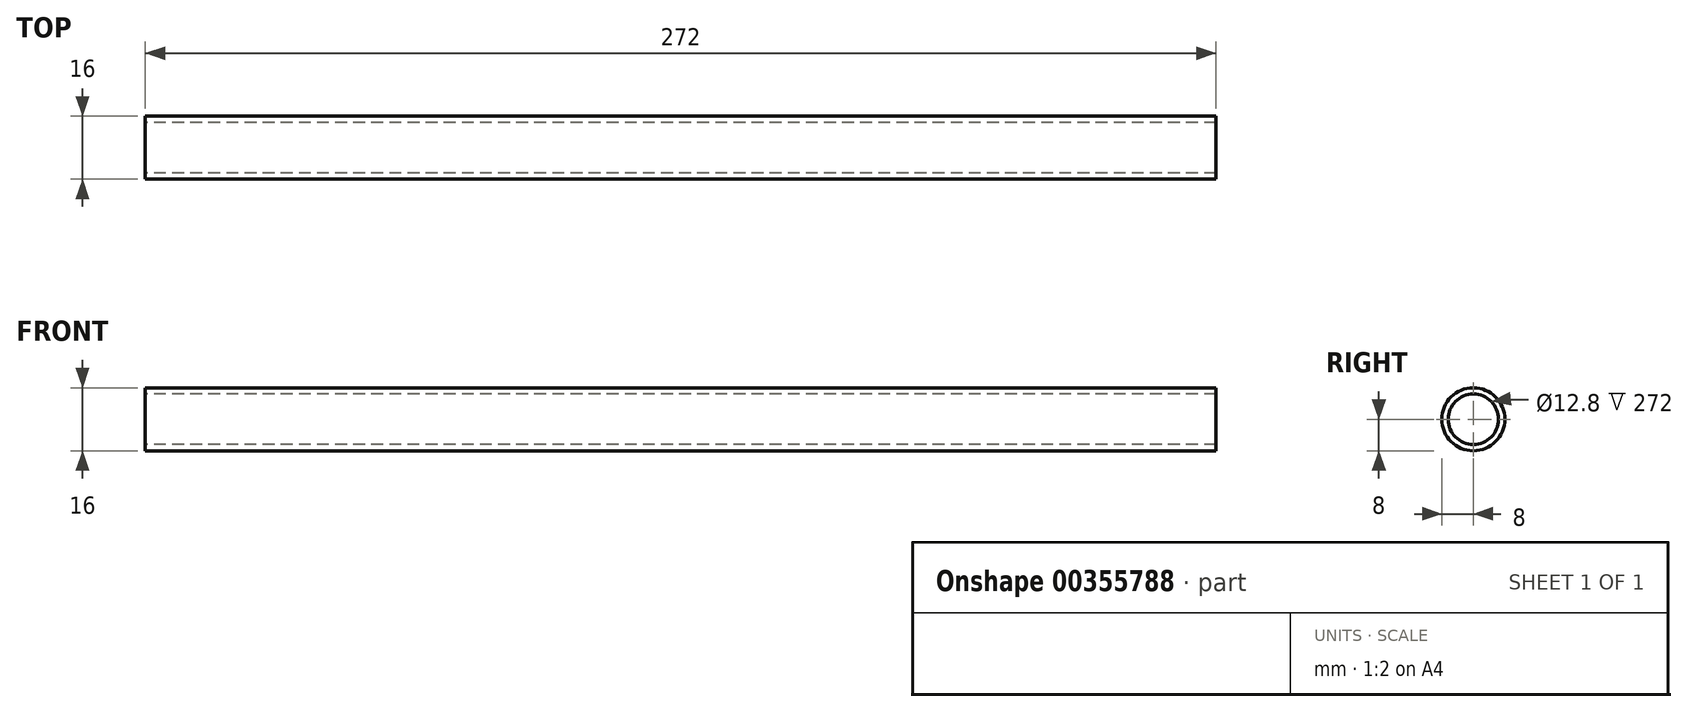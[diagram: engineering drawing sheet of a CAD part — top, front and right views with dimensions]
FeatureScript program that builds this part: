
annotation { "Feature Type Name" : "Feature", "Feature Type Description" : "" }
export const myFeature = defineFeature(function(context is Context, id is Id, definition is map)
    precondition{}
    {
        {
            var Q0;
            Q0=qCreatedBy(makeId("Right.planeOp"),FACE);
            var sketch = newSketch(context, id + "F0", { "sketchPlane" : qUnion([Q0])});
            skCircle(sketch, "E0", {"center": v(0, 0) * mm, "radius": 8 * mm});
            skCircle(sketch, "E1", {"center": v(0, 0) * mm, "radius": 6.4 * mm});
            skSolve(sketch);
        }
        {
            var Q0;
            Q0=qSketchRegion(id+"F0",true);
            extrude(context, id + "F1", {"entities" : qUnion([Q0]), "depth" : 136 * mm, "hasSecondDirection" : true, "secondDirectionOppositeDirection" : true, "secondDirectionDepth" : 136 * mm});
        }
    });
